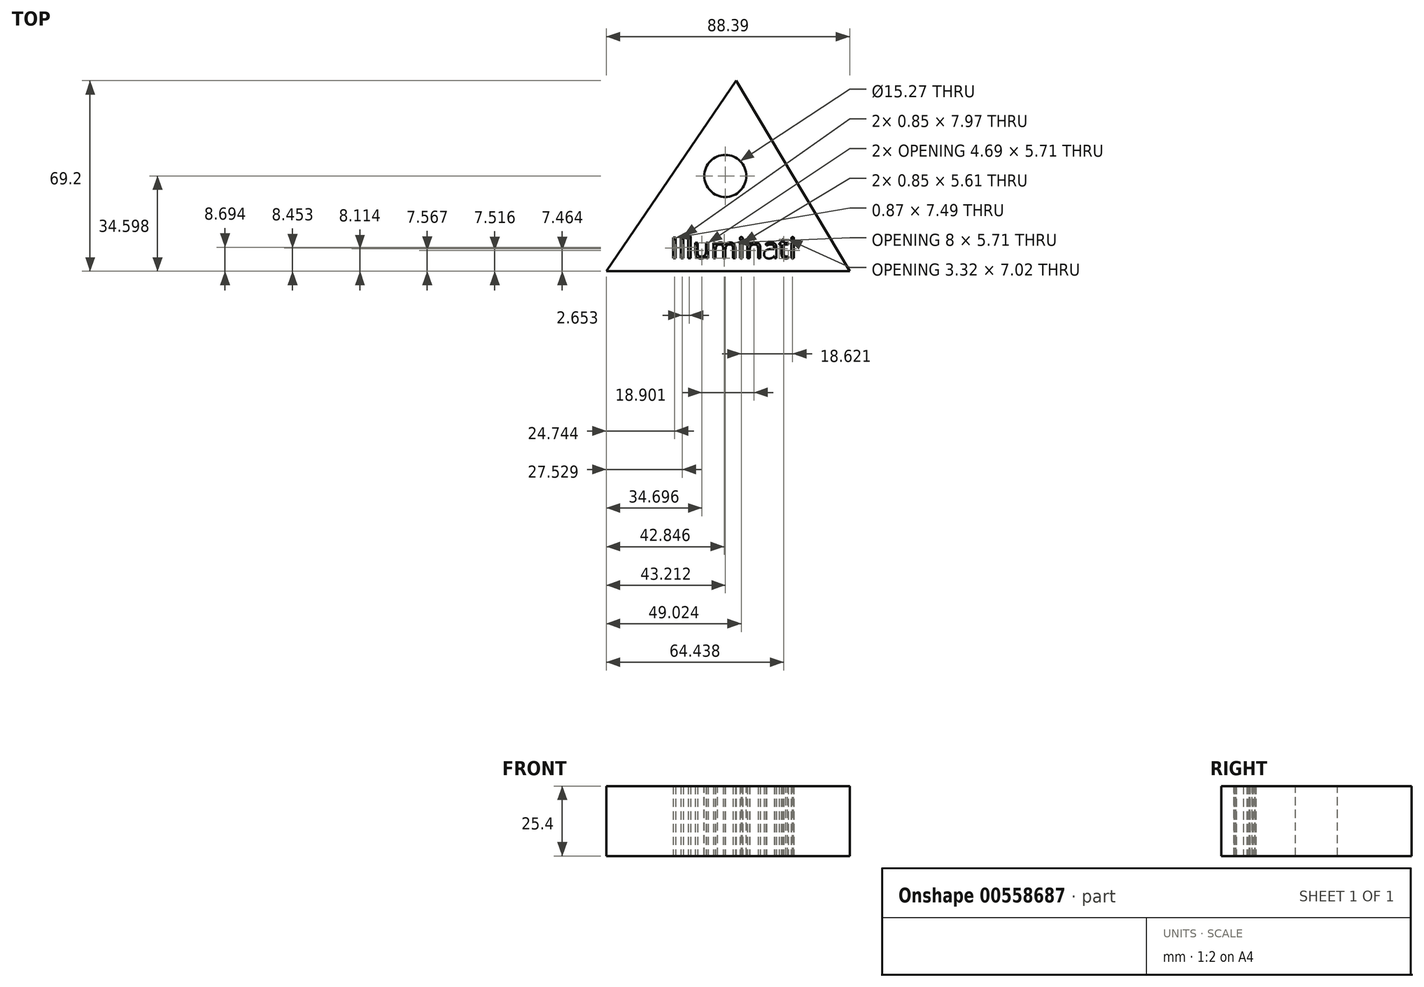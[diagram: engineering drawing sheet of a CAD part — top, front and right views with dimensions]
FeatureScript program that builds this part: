
annotation { "Feature Type Name" : "Feature", "Feature Type Description" : "" }
export const myFeature = defineFeature(function(context is Context, id is Id, definition is map)
    precondition{}
    {
        {
            var Q0;
            Q0=qCreatedBy(makeId("Top.planeOp"),FACE);
            var sketch = newSketch(context, id + "F0", { "sketchPlane" : qUnion([Q0])});
            skLineSegment(sketch, "E0", {"start": v(0, 46.87) * mm, "end": v(-47.18, -22.33) * mm});
            skLineSegment(sketch, "E1", {"start": v(0, 46.87) * mm, "end": v(41.2, -22.33) * mm});
            skLineSegment(sketch, "E2", {"start": v(-47.18, -22.33) * mm, "end": v(41.2, -22.33) * mm});
            skText(sketch, "E3", { "text": "Illuminati\n", "fontName": "OpenSans-Regular.ttf"});
            const initialGuessF0  = {"E3": [-0.0239, -0.01762, 1, 0, 0.00755]};
            skSetInitialGuess(sketch, initialGuessF0);
            skSolve(sketch);
        }
        {
            var Q0;
            Q0=makeQuery(id+"F0.imprint","IMPRINT",FACE,{"disambiguationData":[TD([[makeQuery(id+"F0.imprint","IMPRINT",EDGE,{"derivedFrom":sQuery(id+"F0.wireOp",EDGE,"E0")}),1.0]])]});
            extrude(context, id + "F1", {"entities" : qUnion([Q0]), "depth" : 25.4 * mm, "offsetDistance" : 25.4 * mm});
        }
        {
            var Q0;
            Q0=makeQuery(id+"F1.opExtrude","CAP_FACE",FACE,{"disambiguationData":[OSD([sQuery(id+"F0.wireOp",EDGE,"E0"),sQuery(id+"F0.wireOp",EDGE,"E1"),sQuery(id+"F0.wireOp",EDGE,"E2"),sQuery(id+"F0.wireOp",EDGE,"E3.sketch_text.stroke-0"),sQuery(id+"F0.wireOp",EDGE,"E3.sketch_text.stroke-1"),sQuery(id+"F0.wireOp",EDGE,"E3.sketch_text.stroke-2"),sQuery(id+"F0.wireOp",EDGE,"E3.sketch_text.stroke-3"),sQuery(id+"F0.wireOp",EDGE,"E3.sketch_text.stroke-4"),sQuery(id+"F0.wireOp",EDGE,"E3.sketch_text.stroke-5"),sQuery(id+"F0.wireOp",EDGE,"E3.sketch_text.stroke-6"),sQuery(id+"F0.wireOp",EDGE,"E3.sketch_text.stroke-7"),sQuery(id+"F0.wireOp",EDGE,"E3.sketch_text.stroke-8"),sQuery(id+"F0.wireOp",EDGE,"E3.sketch_text.stroke-9"),sQuery(id+"F0.wireOp",EDGE,"E3.sketch_text.stroke-10"),sQuery(id+"F0.wireOp",EDGE,"E3.sketch_text.stroke-11"),sQuery(id+"F0.wireOp",EDGE,"E3.sketch_text.stroke-12"),sQuery(id+"F0.wireOp",EDGE,"E3.sketch_text.stroke-13"),sQuery(id+"F0.wireOp",EDGE,"E3.sketch_text.stroke-14"),sQuery(id+"F0.wireOp",EDGE,"E3.sketch_text.stroke-15"),sQuery(id+"F0.wireOp",EDGE,"E3.sketch_text.stroke-16"),sQuery(id+"F0.wireOp",EDGE,"E3.sketch_text.stroke-17"),sQuery(id+"F0.wireOp",EDGE,"E3.sketch_text.stroke-18"),sQuery(id+"F0.wireOp",EDGE,"E3.sketch_text.stroke-19"),sQuery(id+"F0.wireOp",EDGE,"E3.sketch_text.stroke-20"),sQuery(id+"F0.wireOp",EDGE,"E3.sketch_text.stroke-21"),sQuery(id+"F0.wireOp",EDGE,"E3.sketch_text.stroke-22"),sQuery(id+"F0.wireOp",EDGE,"E3.sketch_text.stroke-23"),sQuery(id+"F0.wireOp",EDGE,"E3.sketch_text.stroke-24"),sQuery(id+"F0.wireOp",EDGE,"E3.sketch_text.stroke-25"),sQuery(id+"F0.wireOp",EDGE,"E3.sketch_text.stroke-26"),sQuery(id+"F0.wireOp",EDGE,"E3.sketch_text.stroke-27"),sQuery(id+"F0.wireOp",EDGE,"E3.sketch_text.stroke-28"),sQuery(id+"F0.wireOp",EDGE,"E3.sketch_text.stroke-29"),sQuery(id+"F0.wireOp",EDGE,"E3.sketch_text.stroke-30"),sQuery(id+"F0.wireOp",EDGE,"E3.sketch_text.stroke-31"),sQuery(id+"F0.wireOp",EDGE,"E3.sketch_text.stroke-32"),sQuery(id+"F0.wireOp",EDGE,"E3.sketch_text.stroke-33"),sQuery(id+"F0.wireOp",EDGE,"E3.sketch_text.stroke-34"),sQuery(id+"F0.wireOp",EDGE,"E3.sketch_text.stroke-35"),sQuery(id+"F0.wireOp",EDGE,"E3.sketch_text.stroke-36"),sQuery(id+"F0.wireOp",EDGE,"E3.sketch_text.stroke-37"),sQuery(id+"F0.wireOp",EDGE,"E3.sketch_text.stroke-38"),sQuery(id+"F0.wireOp",EDGE,"E3.sketch_text.stroke-39"),sQuery(id+"F0.wireOp",EDGE,"E3.sketch_text.stroke-40"),sQuery(id+"F0.wireOp",EDGE,"E3.sketch_text.stroke-41"),sQuery(id+"F0.wireOp",EDGE,"E3.sketch_text.stroke-42"),sQuery(id+"F0.wireOp",EDGE,"E3.sketch_text.stroke-43"),sQuery(id+"F0.wireOp",EDGE,"E3.sketch_text.stroke-44"),sQuery(id+"F0.wireOp",EDGE,"E3.sketch_text.stroke-45"),sQuery(id+"F0.wireOp",EDGE,"E3.sketch_text.stroke-46"),sQuery(id+"F0.wireOp",EDGE,"E3.sketch_text.stroke-47"),sQuery(id+"F0.wireOp",EDGE,"E3.sketch_text.stroke-48"),sQuery(id+"F0.wireOp",EDGE,"E3.sketch_text.stroke-49"),sQuery(id+"F0.wireOp",EDGE,"E3.sketch_text.stroke-50"),sQuery(id+"F0.wireOp",EDGE,"E3.sketch_text.stroke-51"),sQuery(id+"F0.wireOp",EDGE,"E3.sketch_text.stroke-52"),sQuery(id+"F0.wireOp",EDGE,"E3.sketch_text.stroke-53"),sQuery(id+"F0.wireOp",EDGE,"E3.sketch_text.stroke-54"),sQuery(id+"F0.wireOp",EDGE,"E3.sketch_text.stroke-55"),sQuery(id+"F0.wireOp",EDGE,"E3.sketch_text.stroke-56"),sQuery(id+"F0.wireOp",EDGE,"E3.sketch_text.stroke-57"),sQuery(id+"F0.wireOp",EDGE,"E3.sketch_text.stroke-58"),sQuery(id+"F0.wireOp",EDGE,"E3.sketch_text.stroke-59"),sQuery(id+"F0.wireOp",EDGE,"E3.sketch_text.stroke-60"),sQuery(id+"F0.wireOp",EDGE,"E3.sketch_text.stroke-61"),sQuery(id+"F0.wireOp",EDGE,"E3.sketch_text.stroke-62"),sQuery(id+"F0.wireOp",EDGE,"E3.sketch_text.stroke-63"),sQuery(id+"F0.wireOp",EDGE,"E3.sketch_text.stroke-64"),sQuery(id+"F0.wireOp",EDGE,"E3.sketch_text.stroke-65"),sQuery(id+"F0.wireOp",EDGE,"E3.sketch_text.stroke-66"),sQuery(id+"F0.wireOp",EDGE,"E3.sketch_text.stroke-67"),sQuery(id+"F0.wireOp",EDGE,"E3.sketch_text.stroke-68"),sQuery(id+"F0.wireOp",EDGE,"E3.sketch_text.stroke-69"),sQuery(id+"F0.wireOp",EDGE,"E3.sketch_text.stroke-70"),sQuery(id+"F0.wireOp",EDGE,"E3.sketch_text.stroke-71"),sQuery(id+"F0.wireOp",EDGE,"E3.sketch_text.stroke-72"),sQuery(id+"F0.wireOp",EDGE,"E3.sketch_text.stroke-73"),sQuery(id+"F0.wireOp",EDGE,"E3.sketch_text.stroke-74"),sQuery(id+"F0.wireOp",EDGE,"E3.sketch_text.stroke-75"),sQuery(id+"F0.wireOp",EDGE,"E3.sketch_text.stroke-76"),sQuery(id+"F0.wireOp",EDGE,"E3.sketch_text.stroke-77"),sQuery(id+"F0.wireOp",EDGE,"E3.sketch_text.stroke-78"),sQuery(id+"F0.wireOp",EDGE,"E3.sketch_text.stroke-79"),sQuery(id+"F0.wireOp",EDGE,"E3.sketch_text.stroke-80"),sQuery(id+"F0.wireOp",EDGE,"E3.sketch_text.stroke-81"),sQuery(id+"F0.wireOp",EDGE,"E3.sketch_text.stroke-82"),sQuery(id+"F0.wireOp",EDGE,"E3.sketch_text.stroke-83"),sQuery(id+"F0.wireOp",EDGE,"E3.sketch_text.stroke-84"),sQuery(id+"F0.wireOp",EDGE,"E3.sketch_text.stroke-85"),sQuery(id+"F0.wireOp",EDGE,"E3.sketch_text.stroke-86"),sQuery(id+"F0.wireOp",EDGE,"E3.sketch_text.stroke-87"),sQuery(id+"F0.wireOp",EDGE,"E3.sketch_text.stroke-88"),sQuery(id+"F0.wireOp",EDGE,"E3.sketch_text.stroke-89"),sQuery(id+"F0.wireOp",EDGE,"E3.sketch_text.stroke-90"),sQuery(id+"F0.wireOp",EDGE,"E3.sketch_text.stroke-91"),sQuery(id+"F0.wireOp",EDGE,"E3.sketch_text.stroke-92"),sQuery(id+"F0.wireOp",EDGE,"E3.sketch_text.stroke-93"),sQuery(id+"F0.wireOp",EDGE,"E3.sketch_text.stroke-94"),sQuery(id+"F0.wireOp",EDGE,"E3.sketch_text.stroke-95"),sQuery(id+"F0.wireOp",EDGE,"E3.sketch_text.stroke-96"),sQuery(id+"F0.wireOp",EDGE,"E3.sketch_text.stroke-97"),sQuery(id+"F0.wireOp",EDGE,"E3.sketch_text.stroke-98"),sQuery(id+"F0.wireOp",EDGE,"E3.sketch_text.stroke-99"),sQuery(id+"F0.wireOp",EDGE,"E3.sketch_text.stroke-100"),sQuery(id+"F0.wireOp",EDGE,"E3.sketch_text.stroke-101"),sQuery(id+"F0.wireOp",EDGE,"E3.sketch_text.stroke-102"),sQuery(id+"F0.wireOp",EDGE,"E3.sketch_text.stroke-103"),sQuery(id+"F0.wireOp",EDGE,"E3.sketch_text.stroke-104"),sQuery(id+"F0.wireOp",EDGE,"E3.sketch_text.stroke-113"),sQuery(id+"F0.wireOp",EDGE,"E3.sketch_text.stroke-114"),sQuery(id+"F0.wireOp",EDGE,"E3.sketch_text.stroke-115"),sQuery(id+"F0.wireOp",EDGE,"E3.sketch_text.stroke-116"),sQuery(id+"F0.wireOp",EDGE,"E3.sketch_text.stroke-117"),sQuery(id+"F0.wireOp",EDGE,"E3.sketch_text.stroke-118"),sQuery(id+"F0.wireOp",EDGE,"E3.sketch_text.stroke-119"),sQuery(id+"F0.wireOp",EDGE,"E3.sketch_text.stroke-120"),sQuery(id+"F0.wireOp",EDGE,"E3.sketch_text.stroke-121"),sQuery(id+"F0.wireOp",EDGE,"E3.sketch_text.stroke-122"),sQuery(id+"F0.wireOp",EDGE,"E3.sketch_text.stroke-123"),sQuery(id+"F0.wireOp",EDGE,"E3.sketch_text.stroke-124"),sQuery(id+"F0.wireOp",EDGE,"E3.sketch_text.stroke-125"),sQuery(id+"F0.wireOp",EDGE,"E3.sketch_text.stroke-126"),sQuery(id+"F0.wireOp",EDGE,"E3.sketch_text.stroke-127"),sQuery(id+"F0.wireOp",EDGE,"E3.sketch_text.stroke-128"),sQuery(id+"F0.wireOp",EDGE,"E3.sketch_text.stroke-129"),sQuery(id+"F0.wireOp",EDGE,"E3.sketch_text.stroke-130"),sQuery(id+"F0.wireOp",EDGE,"E3.sketch_text.stroke-131"),sQuery(id+"F0.wireOp",EDGE,"E3.sketch_text.stroke-132"),sQuery(id+"F0.wireOp",EDGE,"E3.sketch_text.stroke-133"),sQuery(id+"F0.wireOp",EDGE,"E3.sketch_text.stroke-134"),sQuery(id+"F0.wireOp",EDGE,"E3.sketch_text.stroke-135"),sQuery(id+"F0.wireOp",EDGE,"E3.sketch_text.stroke-136"),sQuery(id+"F0.wireOp",EDGE,"E3.sketch_text.stroke-137"),sQuery(id+"F0.wireOp",EDGE,"E3.sketch_text.stroke-138"),sQuery(id+"F0.wireOp",EDGE,"E3.sketch_text.stroke-139"),sQuery(id+"F0.wireOp",EDGE,"E3.sketch_text.stroke-140"),sQuery(id+"F0.wireOp",EDGE,"E3.sketch_text.stroke-141"),sQuery(id+"F0.wireOp",EDGE,"E3.sketch_text.stroke-142"),sQuery(id+"F0.wireOp",EDGE,"E3.sketch_text.stroke-143")])],"isStart":false});
            var sketch = newSketch(context, id + "F2", { "sketchPlane" : qUnion([Q0])});
            skCircle(sketch, "E4", {"center": v(0, 17.64) * mm, "radius": 8.26 * mm});
            skSolve(sketch);
        }
        {
            var Q0;
            Q0 = qSketchRegion(id + "F2", true);
            extrude(context, id + "F3", {"entities" : qUnion([Q0]), "operationType" : NewBodyOperationType.REMOVE, "oppositeDirection" : true, "depth" : 25.4 * mm, "offsetDistance" : 25.4 * mm});
        }
        {
            var Q0;
            Q0 = qSketchRegion(id + "F0", true);
            extrude(context, id + "F4", {"entities" : qUnion([Q0]), "operationType" : NewBodyOperationType.ADD, "depth" : 25.4 * mm, "offsetDistance" : 25.4 * mm});
        }
        {
            var Q0;
            {var subQ0=sQuery(id+"F0.wireOp",EDGE,"E3.sketch_text.stroke-143");var subQ1=sQuery(id+"F0.wireOp",EDGE,"E3.sketch_text.stroke-142");var subQ2=sQuery(id+"F0.wireOp",EDGE,"E3.sketch_text.stroke-141");var subQ3=sQuery(id+"F0.wireOp",EDGE,"E3.sketch_text.stroke-140");var subQ4=sQuery(id+"F0.wireOp",EDGE,"E3.sketch_text.stroke-139");var subQ5=sQuery(id+"F0.wireOp",EDGE,"E3.sketch_text.stroke-138");var subQ6=sQuery(id+"F0.wireOp",EDGE,"E3.sketch_text.stroke-137");var subQ7=sQuery(id+"F0.wireOp",EDGE,"E3.sketch_text.stroke-136");var subQ8=sQuery(id+"F0.wireOp",EDGE,"E3.sketch_text.stroke-135");var subQ9=sQuery(id+"F0.wireOp",EDGE,"E3.sketch_text.stroke-134");var subQ10=sQuery(id+"F0.wireOp",EDGE,"E3.sketch_text.stroke-133");var subQ11=sQuery(id+"F0.wireOp",EDGE,"E3.sketch_text.stroke-132");var subQ12=sQuery(id+"F0.wireOp",EDGE,"E3.sketch_text.stroke-131");var subQ13=sQuery(id+"F0.wireOp",EDGE,"E3.sketch_text.stroke-130");var subQ14=sQuery(id+"F0.wireOp",EDGE,"E3.sketch_text.stroke-129");var subQ15=sQuery(id+"F0.wireOp",EDGE,"E3.sketch_text.stroke-128");var subQ16=sQuery(id+"F0.wireOp",EDGE,"E3.sketch_text.stroke-127");var subQ17=sQuery(id+"F0.wireOp",EDGE,"E3.sketch_text.stroke-126");var subQ18=sQuery(id+"F0.wireOp",EDGE,"E3.sketch_text.stroke-125");var subQ19=sQuery(id+"F0.wireOp",EDGE,"E3.sketch_text.stroke-124");var subQ20=sQuery(id+"F0.wireOp",EDGE,"E3.sketch_text.stroke-123");var subQ21=sQuery(id+"F0.wireOp",EDGE,"E3.sketch_text.stroke-122");var subQ22=sQuery(id+"F0.wireOp",EDGE,"E3.sketch_text.stroke-121");var subQ23=sQuery(id+"F0.wireOp",EDGE,"E3.sketch_text.stroke-120");var subQ24=sQuery(id+"F0.wireOp",EDGE,"E3.sketch_text.stroke-119");var subQ25=sQuery(id+"F0.wireOp",EDGE,"E3.sketch_text.stroke-118");var subQ26=sQuery(id+"F0.wireOp",EDGE,"E3.sketch_text.stroke-117");var subQ27=sQuery(id+"F0.wireOp",EDGE,"E3.sketch_text.stroke-116");var subQ28=sQuery(id+"F0.wireOp",EDGE,"E3.sketch_text.stroke-115");var subQ29=sQuery(id+"F0.wireOp",EDGE,"E3.sketch_text.stroke-114");var subQ30=sQuery(id+"F0.wireOp",EDGE,"E3.sketch_text.stroke-113");var subQ31=sQuery(id+"F0.wireOp",EDGE,"E3.sketch_text.stroke-104");var subQ32=sQuery(id+"F0.wireOp",EDGE,"E3.sketch_text.stroke-103");var subQ33=sQuery(id+"F0.wireOp",EDGE,"E3.sketch_text.stroke-102");var subQ34=sQuery(id+"F0.wireOp",EDGE,"E3.sketch_text.stroke-101");var subQ35=sQuery(id+"F0.wireOp",EDGE,"E3.sketch_text.stroke-100");var subQ36=sQuery(id+"F0.wireOp",EDGE,"E3.sketch_text.stroke-99");var subQ37=sQuery(id+"F0.wireOp",EDGE,"E3.sketch_text.stroke-98");var subQ38=sQuery(id+"F0.wireOp",EDGE,"E3.sketch_text.stroke-97");var subQ39=sQuery(id+"F0.wireOp",EDGE,"E3.sketch_text.stroke-96");var subQ40=sQuery(id+"F0.wireOp",EDGE,"E3.sketch_text.stroke-95");var subQ41=sQuery(id+"F0.wireOp",EDGE,"E3.sketch_text.stroke-94");var subQ42=sQuery(id+"F0.wireOp",EDGE,"E3.sketch_text.stroke-93");var subQ43=sQuery(id+"F0.wireOp",EDGE,"E3.sketch_text.stroke-92");var subQ44=sQuery(id+"F0.wireOp",EDGE,"E3.sketch_text.stroke-91");var subQ45=sQuery(id+"F0.wireOp",EDGE,"E3.sketch_text.stroke-90");var subQ46=sQuery(id+"F0.wireOp",EDGE,"E3.sketch_text.stroke-89");var subQ47=sQuery(id+"F0.wireOp",EDGE,"E3.sketch_text.stroke-88");var subQ48=sQuery(id+"F0.wireOp",EDGE,"E3.sketch_text.stroke-87");var subQ49=sQuery(id+"F0.wireOp",EDGE,"E3.sketch_text.stroke-86");var subQ50=sQuery(id+"F0.wireOp",EDGE,"E3.sketch_text.stroke-85");var subQ51=sQuery(id+"F0.wireOp",EDGE,"E3.sketch_text.stroke-84");var subQ52=sQuery(id+"F0.wireOp",EDGE,"E3.sketch_text.stroke-83");var subQ53=sQuery(id+"F0.wireOp",EDGE,"E3.sketch_text.stroke-82");var subQ54=sQuery(id+"F0.wireOp",EDGE,"E3.sketch_text.stroke-81");var subQ55=sQuery(id+"F0.wireOp",EDGE,"E3.sketch_text.stroke-80");var subQ56=sQuery(id+"F0.wireOp",EDGE,"E3.sketch_text.stroke-79");var subQ57=sQuery(id+"F0.wireOp",EDGE,"E3.sketch_text.stroke-78");var subQ58=sQuery(id+"F0.wireOp",EDGE,"E3.sketch_text.stroke-77");var subQ59=sQuery(id+"F0.wireOp",EDGE,"E3.sketch_text.stroke-76");var subQ60=sQuery(id+"F0.wireOp",EDGE,"E3.sketch_text.stroke-75");var subQ61=sQuery(id+"F0.wireOp",EDGE,"E3.sketch_text.stroke-74");var subQ62=sQuery(id+"F0.wireOp",EDGE,"E3.sketch_text.stroke-73");var subQ63=sQuery(id+"F0.wireOp",EDGE,"E3.sketch_text.stroke-72");var subQ64=sQuery(id+"F0.wireOp",EDGE,"E3.sketch_text.stroke-71");var subQ65=sQuery(id+"F0.wireOp",EDGE,"E3.sketch_text.stroke-70");var subQ66=sQuery(id+"F0.wireOp",EDGE,"E3.sketch_text.stroke-69");var subQ67=sQuery(id+"F0.wireOp",EDGE,"E3.sketch_text.stroke-68");var subQ68=sQuery(id+"F0.wireOp",EDGE,"E3.sketch_text.stroke-67");var subQ69=sQuery(id+"F0.wireOp",EDGE,"E3.sketch_text.stroke-66");var subQ70=sQuery(id+"F0.wireOp",EDGE,"E3.sketch_text.stroke-65");var subQ71=sQuery(id+"F0.wireOp",EDGE,"E3.sketch_text.stroke-64");var subQ72=sQuery(id+"F0.wireOp",EDGE,"E3.sketch_text.stroke-63");var subQ73=sQuery(id+"F0.wireOp",EDGE,"E3.sketch_text.stroke-62");var subQ74=sQuery(id+"F0.wireOp",EDGE,"E3.sketch_text.stroke-61");var subQ75=sQuery(id+"F0.wireOp",EDGE,"E3.sketch_text.stroke-60");var subQ76=sQuery(id+"F0.wireOp",EDGE,"E3.sketch_text.stroke-59");var subQ77=sQuery(id+"F0.wireOp",EDGE,"E3.sketch_text.stroke-58");var subQ78=sQuery(id+"F0.wireOp",EDGE,"E3.sketch_text.stroke-57");var subQ79=sQuery(id+"F0.wireOp",EDGE,"E3.sketch_text.stroke-56");var subQ80=sQuery(id+"F0.wireOp",EDGE,"E3.sketch_text.stroke-55");var subQ81=sQuery(id+"F0.wireOp",EDGE,"E3.sketch_text.stroke-54");var subQ82=sQuery(id+"F0.wireOp",EDGE,"E3.sketch_text.stroke-53");var subQ83=sQuery(id+"F0.wireOp",EDGE,"E3.sketch_text.stroke-52");var subQ84=sQuery(id+"F0.wireOp",EDGE,"E3.sketch_text.stroke-51");var subQ85=sQuery(id+"F0.wireOp",EDGE,"E3.sketch_text.stroke-50");var subQ86=sQuery(id+"F0.wireOp",EDGE,"E3.sketch_text.stroke-49");var subQ87=sQuery(id+"F0.wireOp",EDGE,"E3.sketch_text.stroke-48");var subQ88=sQuery(id+"F0.wireOp",EDGE,"E3.sketch_text.stroke-47");var subQ89=sQuery(id+"F0.wireOp",EDGE,"E3.sketch_text.stroke-46");var subQ90=sQuery(id+"F0.wireOp",EDGE,"E3.sketch_text.stroke-45");var subQ91=sQuery(id+"F0.wireOp",EDGE,"E3.sketch_text.stroke-44");var subQ92=sQuery(id+"F0.wireOp",EDGE,"E3.sketch_text.stroke-43");var subQ93=sQuery(id+"F0.wireOp",EDGE,"E3.sketch_text.stroke-42");var subQ94=sQuery(id+"F0.wireOp",EDGE,"E3.sketch_text.stroke-41");var subQ95=sQuery(id+"F0.wireOp",EDGE,"E3.sketch_text.stroke-40");var subQ96=sQuery(id+"F0.wireOp",EDGE,"E3.sketch_text.stroke-39");var subQ97=sQuery(id+"F0.wireOp",EDGE,"E3.sketch_text.stroke-38");var subQ98=sQuery(id+"F0.wireOp",EDGE,"E3.sketch_text.stroke-37");var subQ99=sQuery(id+"F0.wireOp",EDGE,"E3.sketch_text.stroke-36");var subQ100=sQuery(id+"F0.wireOp",EDGE,"E3.sketch_text.stroke-35");var subQ101=sQuery(id+"F0.wireOp",EDGE,"E3.sketch_text.stroke-34");var subQ102=sQuery(id+"F0.wireOp",EDGE,"E3.sketch_text.stroke-33");var subQ103=sQuery(id+"F0.wireOp",EDGE,"E3.sketch_text.stroke-32");var subQ104=sQuery(id+"F0.wireOp",EDGE,"E3.sketch_text.stroke-31");var subQ105=sQuery(id+"F0.wireOp",EDGE,"E3.sketch_text.stroke-30");var subQ106=sQuery(id+"F0.wireOp",EDGE,"E3.sketch_text.stroke-29");var subQ107=sQuery(id+"F0.wireOp",EDGE,"E3.sketch_text.stroke-28");var subQ108=sQuery(id+"F0.wireOp",EDGE,"E3.sketch_text.stroke-27");var subQ109=sQuery(id+"F0.wireOp",EDGE,"E3.sketch_text.stroke-26");var subQ110=sQuery(id+"F0.wireOp",EDGE,"E3.sketch_text.stroke-25");var subQ111=sQuery(id+"F0.wireOp",EDGE,"E3.sketch_text.stroke-24");var subQ112=sQuery(id+"F0.wireOp",EDGE,"E3.sketch_text.stroke-23");var subQ113=sQuery(id+"F0.wireOp",EDGE,"E3.sketch_text.stroke-22");var subQ114=sQuery(id+"F0.wireOp",EDGE,"E3.sketch_text.stroke-21");var subQ115=sQuery(id+"F0.wireOp",EDGE,"E3.sketch_text.stroke-20");var subQ116=sQuery(id+"F0.wireOp",EDGE,"E3.sketch_text.stroke-19");var subQ117=sQuery(id+"F0.wireOp",EDGE,"E3.sketch_text.stroke-18");var subQ118=sQuery(id+"F0.wireOp",EDGE,"E3.sketch_text.stroke-17");var subQ119=sQuery(id+"F0.wireOp",EDGE,"E3.sketch_text.stroke-16");var subQ120=sQuery(id+"F0.wireOp",EDGE,"E3.sketch_text.stroke-15");var subQ121=sQuery(id+"F0.wireOp",EDGE,"E3.sketch_text.stroke-14");var subQ122=sQuery(id+"F0.wireOp",EDGE,"E3.sketch_text.stroke-13");var subQ123=sQuery(id+"F0.wireOp",EDGE,"E3.sketch_text.stroke-12");var subQ124=sQuery(id+"F0.wireOp",EDGE,"E3.sketch_text.stroke-11");var subQ125=sQuery(id+"F0.wireOp",EDGE,"E3.sketch_text.stroke-10");var subQ126=sQuery(id+"F0.wireOp",EDGE,"E3.sketch_text.stroke-9");var subQ127=sQuery(id+"F0.wireOp",EDGE,"E3.sketch_text.stroke-8");var subQ128=sQuery(id+"F0.wireOp",EDGE,"E3.sketch_text.stroke-7");var subQ129=sQuery(id+"F0.wireOp",EDGE,"E3.sketch_text.stroke-6");var subQ130=sQuery(id+"F0.wireOp",EDGE,"E3.sketch_text.stroke-5");var subQ131=sQuery(id+"F0.wireOp",EDGE,"E3.sketch_text.stroke-4");var subQ132=sQuery(id+"F0.wireOp",EDGE,"E3.sketch_text.stroke-3");var subQ133=sQuery(id+"F0.wireOp",EDGE,"E3.sketch_text.stroke-2");var subQ134=sQuery(id+"F0.wireOp",EDGE,"E3.sketch_text.stroke-1");var subQ135=sQuery(id+"F0.wireOp",EDGE,"E3.sketch_text.stroke-0");var subQ136=sQuery(id+"F0.wireOp",EDGE,"E2");var subQ137=sQuery(id+"F0.wireOp",EDGE,"E1");var subQ138=sQuery(id+"F0.wireOp",EDGE,"E0");Q0=makeQuery(id+"F4.boolean.opBoolean","MERGE",FACE,{"derivedFrom":[makeQuery(id+"F1.opExtrude","CAP_FACE",FACE,{"disambiguationData":[OSD([subQ138,subQ137,subQ136,subQ135,subQ134,subQ133,subQ132,subQ131,subQ130,subQ129,subQ128,subQ127,subQ126,subQ125,subQ124,subQ123,subQ122,subQ121,subQ120,subQ119,subQ118,subQ117,subQ116,subQ115,subQ114,subQ113,subQ112,subQ111,subQ110,subQ109,subQ108,subQ107,subQ106,subQ105,subQ104,subQ103,subQ102,subQ101,subQ100,subQ99,subQ98,subQ97,subQ96,subQ95,subQ94,subQ93,subQ92,subQ91,subQ90,subQ89,subQ88,subQ87,subQ86,subQ85,subQ84,subQ83,subQ82,subQ81,subQ80,subQ79,subQ78,subQ77,subQ76,subQ75,subQ74,subQ73,subQ72,subQ71,subQ70,subQ69,subQ68,subQ67,subQ66,subQ65,subQ64,subQ63,subQ62,subQ61,subQ60,subQ59,subQ58,subQ57,subQ56,subQ55,subQ54,subQ53,subQ52,subQ51,subQ50,subQ49,subQ48,subQ47,subQ46,subQ45,subQ44,subQ43,subQ42,subQ41,subQ40,subQ39,subQ38,subQ37,subQ36,subQ35,subQ34,subQ33,subQ32,subQ31,subQ30,subQ29,subQ28,subQ27,subQ26,subQ25,subQ24,subQ23,subQ22,subQ21,subQ20,subQ19,subQ18,subQ17,subQ16,subQ15,subQ14,subQ13,subQ12,subQ11,subQ10,subQ9,subQ8,subQ7,subQ6,subQ5,subQ4,subQ3,subQ2,subQ1,subQ0])],"isStart":false}),makeQuery(id+"F4.opExtrude","CAP_FACE",FACE,{"disambiguationData":[OSD([subQ138,subQ137,subQ136,subQ135,subQ134,subQ133,subQ132,subQ131,subQ130,subQ129,subQ128,subQ127,subQ126,subQ125,subQ124,subQ123,subQ122,subQ121,subQ120,subQ119,subQ118,subQ117,subQ116,subQ115,subQ114,subQ113,subQ112,subQ111,subQ110,subQ109,subQ108,subQ107,subQ106,subQ105,subQ104,subQ103,subQ102,subQ101,subQ100,subQ99,subQ98,subQ97,subQ96,subQ95,subQ94,subQ93,subQ92,subQ91,subQ90,subQ89,subQ88,subQ87,subQ86,subQ85,subQ84,subQ83,subQ82,subQ81,subQ80,subQ79,subQ78,subQ77,subQ76,subQ75,subQ74,subQ73,subQ72,subQ71,subQ70,subQ69,subQ68,subQ67,subQ66,subQ65,subQ64,subQ63,subQ62,subQ61,subQ60,subQ59,subQ58,subQ57,subQ56,subQ55,subQ54,subQ53,subQ52,subQ51,subQ50,subQ49,subQ48,subQ47,subQ46,subQ45,subQ44,subQ43,subQ42,subQ41,subQ40,subQ39,subQ38,subQ37,subQ36,subQ35,subQ34,subQ33,subQ32,subQ31,subQ30,subQ29,subQ28,subQ27,subQ26,subQ25,subQ24,subQ23,subQ22,subQ21,subQ20,subQ19,subQ18,subQ17,subQ16,subQ15,subQ14,subQ13,subQ12,subQ11,subQ10,subQ9,subQ8,subQ7,subQ6,subQ5,subQ4,subQ3,subQ2,subQ1,subQ0])],"isStart":false})]});}
            var sketch = newSketch(context, id + "F5", { "sketchPlane" : qUnion([Q0])});
            skCircle(sketch, "E5", {"center": v(-3.97, 12.27) * mm, "radius": 7.63 * mm});
            skPoint(sketch, "E5.centerSnap0", {"position": v(20.6, 12.27) * mm});
            skSolve(sketch);
        }
        {
            var Q0;
            Q0 = qSketchRegion(id + "F5", true);
            extrude(context, id + "F6", {"entities" : qUnion([Q0]), "operationType" : NewBodyOperationType.REMOVE, "oppositeDirection" : true, "depth" : 25.4 * mm, "offsetDistance" : 25.4 * mm});
        }
    });
